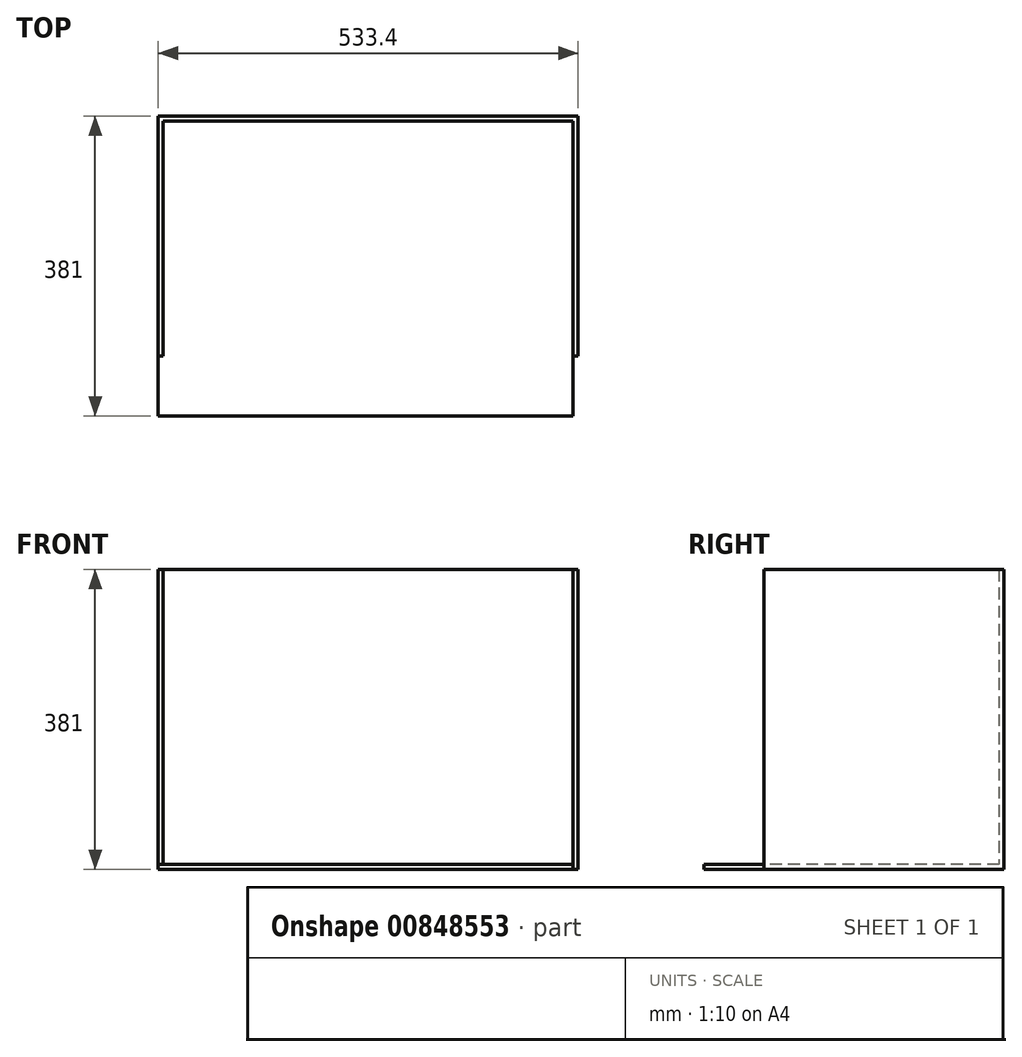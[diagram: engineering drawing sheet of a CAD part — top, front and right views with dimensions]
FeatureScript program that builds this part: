
annotation { "Feature Type Name" : "Feature", "Feature Type Description" : "" }
export const myFeature = defineFeature(function(context is Context, id is Id, definition is map)
    precondition{}
    {
        {
            var Q0;
            Q0=qCreatedBy(makeId("Top.planeOp"),FACE);
            var sketch = newSketch(context, id + "F0", { "sketchPlane" : qUnion([Q0])});
            skLineSegment(sketch, "E0.bottom", {"start": v(486.6, 244.42) * mm, "end": v(-46.8, 244.42) * mm});
            skLineSegment(sketch, "E0.top", {"start": v(486.6, -60.38) * mm, "end": v(-46.8, -60.38) * mm});
            skLineSegment(sketch, "E0.left", {"start": v(486.6, 244.42) * mm, "end": v(486.6, -60.38) * mm});
            skLineSegment(sketch, "E0.right", {"start": v(-46.8, 244.42) * mm, "end": v(-46.8, -60.38) * mm});
            skSolve(sketch);
        }
        {
            var Q0;
            Q0 = qSketchRegion(id + "F0", true);
            extrude(context, id + "F1", {"entities" : qUnion([Q0]), "depth" : 381 * mm, "offsetDistance" : 25.4 * mm});
        }
        {
            var Q0;
            Q0=makeQuery(id+"F1.opExtrude","CAP_FACE",FACE,{"disambiguationData":[OSD([sQuery(id+"F0.wireOp",EDGE,"E0.bottom"),sQuery(id+"F0.wireOp",EDGE,"E0.top"),sQuery(id+"F0.wireOp",EDGE,"E0.left"),sQuery(id+"F0.wireOp",EDGE,"E0.right")])],"isStart":false});
            var Q1;
            Q1=makeQuery(id+"F1.opExtrude","SWEPT_FACE",FACE,{"disambiguationData":[OSD([sQuery(id+"F0.wireOp",EDGE,"E0.top")])]});
            shell(context, id + "F2", {"entities" : qUnion([Q0, Q1]), "thickness" : 6.35 * mm});
        }
        {
            var Q0;
            Q0=makeQuery(id+"F1.opExtrude","SWEPT_FACE",FACE,{"disambiguationData":[OSD([sQuery(id+"F0.wireOp",EDGE,"E0.top")])]});
            var sketch = newSketch(context, id + "F3", { "sketchPlane" : qUnion([Q0])});
            skLineSegment(sketch, "E1.bottom", {"start": v(-46.8, 0) * mm, "end": v(480.25, 0) * mm});
            skLineSegment(sketch, "E1.top", {"start": v(-46.8, 6.35) * mm, "end": v(480.25, 6.35) * mm});
            skLineSegment(sketch, "E1.left", {"start": v(-46.8, 0) * mm, "end": v(-46.8, 6.35) * mm});
            skLineSegment(sketch, "E1.right", {"start": v(480.25, 0) * mm, "end": v(480.25, 6.35) * mm});
            skSolve(sketch);
        }
        {
            var Q0;
            Q0 = qSketchRegion(id + "F3", true);
            extrude(context, id + "F4", {"entities" : qUnion([Q0]), "operationType" : NewBodyOperationType.ADD, "depth" : 76.2 * mm, "offsetDistance" : 25.4 * mm});
        }
    });
